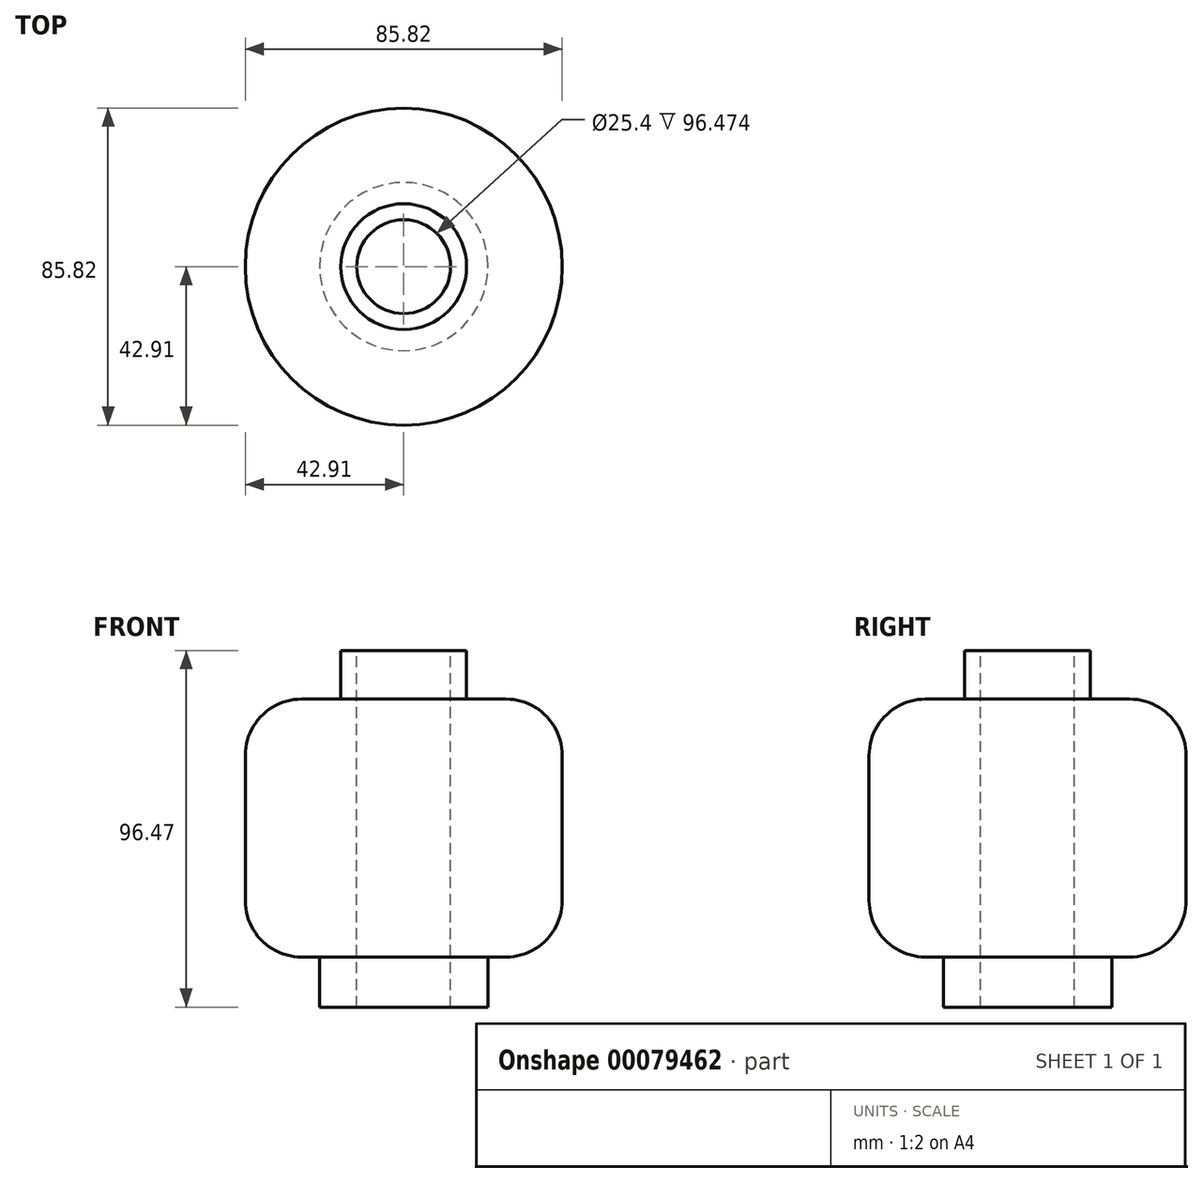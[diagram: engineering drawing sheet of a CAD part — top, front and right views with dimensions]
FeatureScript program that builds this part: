
annotation { "Feature Type Name" : "Feature", "Feature Type Description" : "" }
export const myFeature = defineFeature(function(context is Context, id is Id, definition is map)
    precondition{}
    {
        {
            var Q0;
            Q0=qCreatedBy(makeId("Top.planeOp"),FACE);
            var sketch = newSketch(context, id + "F0", { "sketchPlane" : qUnion([Q0])});
            skCircle(sketch, "E0", {"center": v(0, 0) * mm, "radius": 22.77 * mm});
            skSolve(sketch);
        }
        {
            var Q0;
            Q0=makeQuery(id+"F0.imprint","IMPRINT",FACE,{"disambiguationData":[TD([[makeQuery(id+"F0.imprint","IMPRINT",EDGE,{"derivedFrom":sQuery(id+"F0.wireOp",EDGE,"E0")}),1.0]])]});
            extrude(context, id + "F1", {"entities" : qUnion([Q0]), "depth" : 13.56 * mm});
        }
        {
            var Q0;
            Q0=makeQuery(id+"F1.opExtrude","CAP_FACE",FACE,{"disambiguationData":[OSD([sQuery(id+"F0.wireOp",EDGE,"E0")])],"isStart":false});
            var sketch = newSketch(context, id + "F2", { "sketchPlane" : qUnion([Q0])});
            skCircle(sketch, "E1", {"center": v(0, 0) * mm, "radius": 42.9 * mm});
            skSolve(sketch);
        }
        {
            var Q0;
            Q0=makeQuery(id+"F2.imprint","IMPRINT",FACE,{"disambiguationData":[TD([[makeQuery(id+"F2.imprint","IMPRINT",EDGE,{"derivedFrom":sQuery(id+"F2.wireOp",EDGE,"E1")}),1.0]])]});
            var Q1;
            Q1=makeQuery(id+"F2.imprint","IMPRINT",FACE,{"disambiguationData":[TD([[makeQuery(id+"F2.imprint","IMPRINT",EDGE,{"derivedFrom":makeQuery(id+"F1.opExtrude","CAP_EDGE",EDGE,{"disambiguationData":[OSD([sQuery(id+"F0.wireOp",EDGE,"E0")])],"isStart":false})}),1.0]])]});
            extrude(context, id + "F3", {"entities" : qUnion([Q0, Q1]), "operationType" : NewBodyOperationType.ADD, "depth" : 69.8 * mm});
        }
        {
            var Q0;
            Q0=makeQuery(id+"F3.opExtrude","CAP_FACE",FACE,{"disambiguationData":[OSD([sQuery(id+"F2.wireOp",EDGE,"E1")])],"isStart":false});
            var sketch = newSketch(context, id + "F4", { "sketchPlane" : qUnion([Q0])});
            skCircle(sketch, "E2", {"center": v(0, 0) * mm, "radius": 17.02 * mm});
            skSolve(sketch);
        }
        {
            var Q0;
            Q0=makeQuery(id+"F4.imprint","IMPRINT",FACE,{"disambiguationData":[TD([[makeQuery(id+"F4.imprint","IMPRINT",EDGE,{"derivedFrom":sQuery(id+"F4.wireOp",EDGE,"E2")}),1.0]])]});
            extrude(context, id + "F5", {"entities" : qUnion([Q0]), "operationType" : NewBodyOperationType.ADD, "depth" : 13.1 * mm});
        }
        {
            var Q0;
            Q0=makeQuery(id+"F3.opExtrude","CAP_EDGE",EDGE,{"disambiguationData":[OSD([sQuery(id+"F2.wireOp",EDGE,"E1")])],"isStart":false});
            var Q1;
            Q1=makeQuery(id+"F3.opExtrude","CAP_EDGE",EDGE,{"disambiguationData":[OSD([sQuery(id+"F2.wireOp",EDGE,"E1")])],"isStart":true});
            fillet(context, id + "F6", {"entities" : qUnion([Q0, Q1]), "radius" : 15.24 * mm, "tangentPropagation" : true, "allowEdgeOverflow" : false});
        }
        {
            var Q0;
            Q0=makeQuery(id+"F5.opExtrude","CAP_FACE",FACE,{"disambiguationData":[OSD([sQuery(id+"F4.wireOp",EDGE,"E2")])],"isStart":false});
            var sketch = newSketch(context, id + "F7", { "sketchPlane" : qUnion([Q0])});
            skCircle(sketch, "E3", {"center": v(0, 0) * mm, "radius": 9.13 * mm});
            skSolve(sketch);
        }
        {
            var Q0;
            Q0=sQuery(id+"F7.wireOp",VERTEX,"E3.center");
            var Q1;
            Q1=makeQuery(id+"F1.opExtrude","SWEPT_BODY",BODY,{"disambiguationData":[OSD([sQuery(id+"F0.wireOp",EDGE,"E0")])]});
            hole(context, id + "F8", {"style" : HoleStyle.SIMPLE, "endStyle" : HoleEndStyle.THROUGH, "holeDiameter" : 25.4 * mm, "locations" : qUnion([Q0]), "scope" : qUnion([Q1]), "isTappedThrough" : true});
        }
    });
